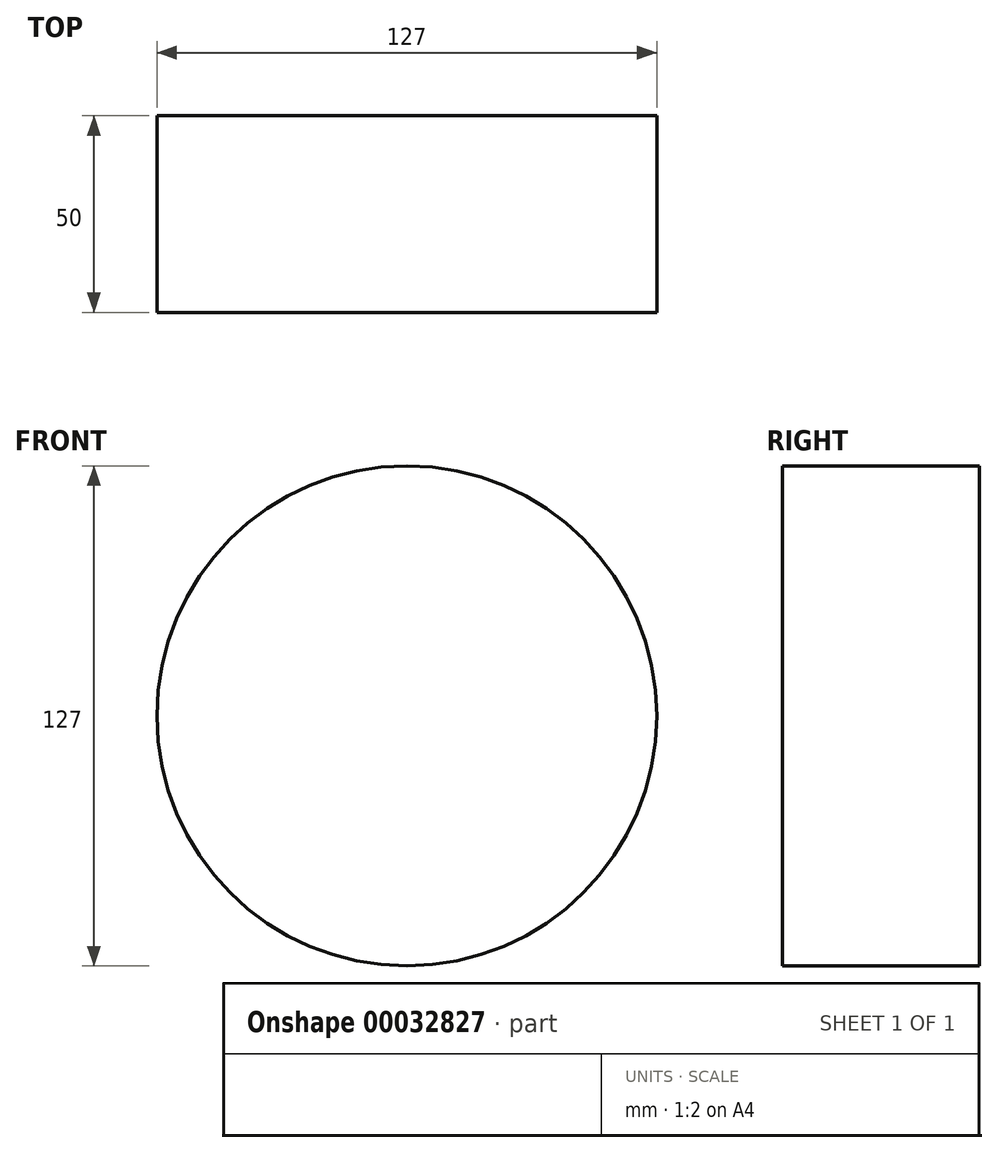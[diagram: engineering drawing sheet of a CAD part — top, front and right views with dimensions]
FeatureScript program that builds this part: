
annotation { "Feature Type Name" : "Feature", "Feature Type Description" : "" }
export const myFeature = defineFeature(function(context is Context, id is Id, definition is map)
    precondition{}
    {
        {
            var Q0;
            Q0=qCreatedBy(makeId("Front.planeOp"),FACE);
            var sketch = newSketch(context, id + "F0", { "sketchPlane" : qUnion([Q0])});
            skCircle(sketch, "E0", {"center": v(0, 0) * mm, "radius": 63.5 * mm});
            skSolve(sketch);
        }
        {
            var Q0;
            Q0=makeQuery(id+"F0.imprint","IMPRINT",FACE,{"disambiguationData":[TD([[makeQuery(id+"F0.imprint","IMPRINT",EDGE,{"derivedFrom":sQuery(id+"F0.wireOp",EDGE,"E0")}),1.0]])]});
            extrude(context, id + "F1", {"entities" : qUnion([Q0]), "depth" : 50 * mm});
        }
    });
